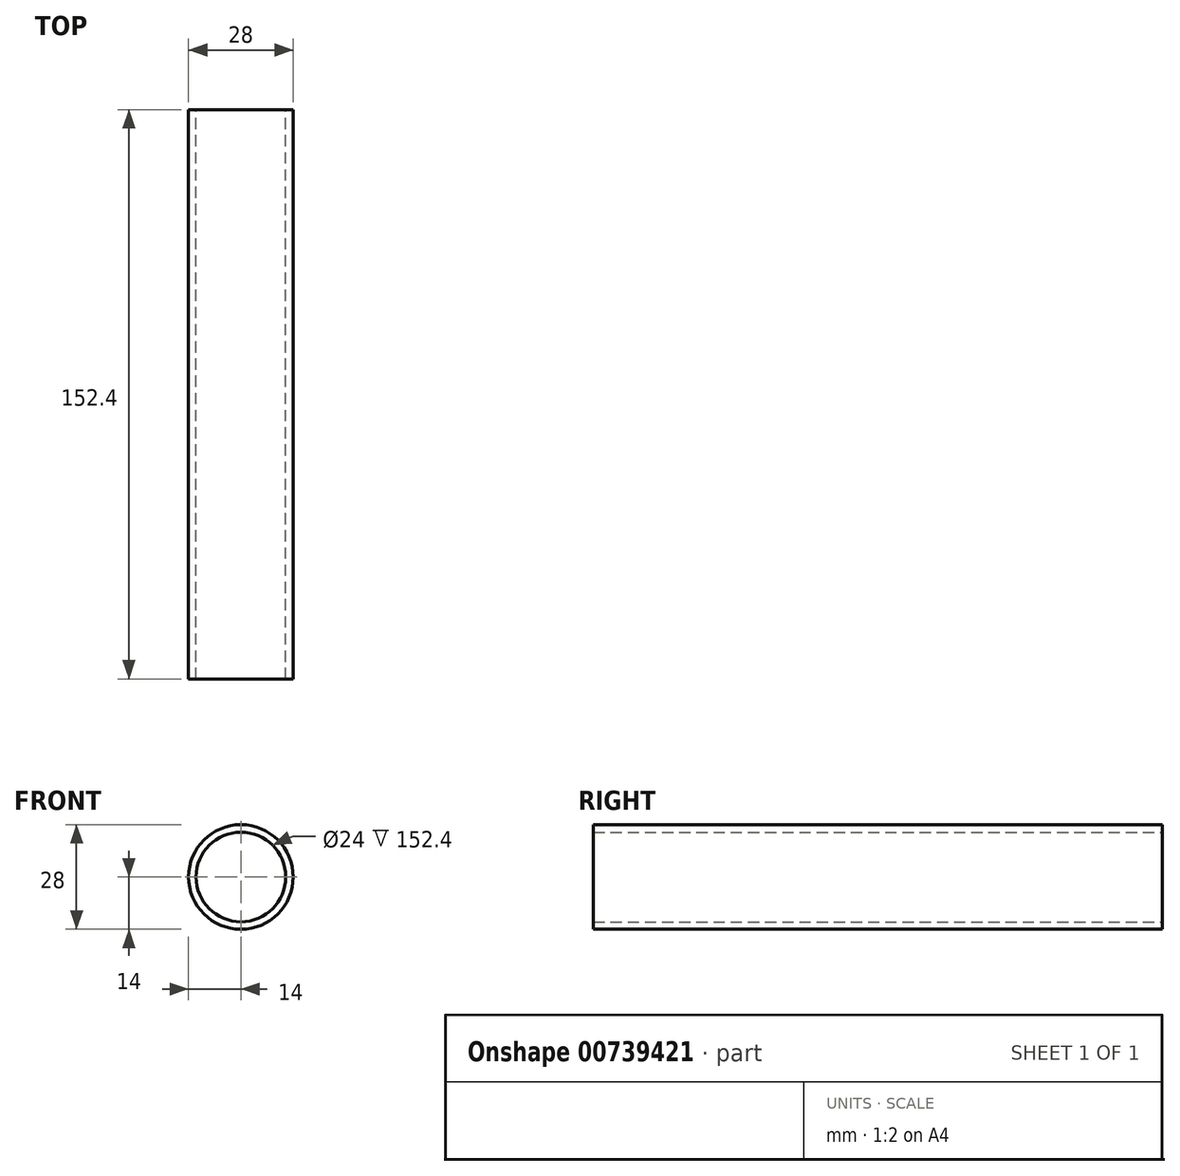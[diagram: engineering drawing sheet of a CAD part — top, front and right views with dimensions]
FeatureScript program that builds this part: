
annotation { "Feature Type Name" : "Feature", "Feature Type Description" : "" }
export const myFeature = defineFeature(function(context is Context, id is Id, definition is map)
    precondition{}
    {
        {
            var Q0;
            Q0=qCreatedBy(makeId("Front.planeOp"),FACE);
            var sketch = newSketch(context, id + "F0", { "sketchPlane" : qUnion([Q0])});
            skCircle(sketch, "E0", {"center": v(0, 0) * mm, "radius": 12 * mm});
            skCircle(sketch, "E1", {"center": v(0, 0) * mm, "radius": 14 * mm});
            skSolve(sketch);
        }
        {
            var Q0;
            Q0=makeQuery(id+"F0.imprint","IMPRINT",FACE,{"disambiguationData":[TD([[makeQuery(id+"F0.imprint","IMPRINT",EDGE,{"derivedFrom":sQuery(id+"F0.wireOp",EDGE,"E0")}),-1.0]])]});
            extrude(context, id + "F1", {"entities" : qUnion([Q0]), "depth" : 152.4 * mm, "offsetDistance" : 25.4 * mm});
        }
    });
